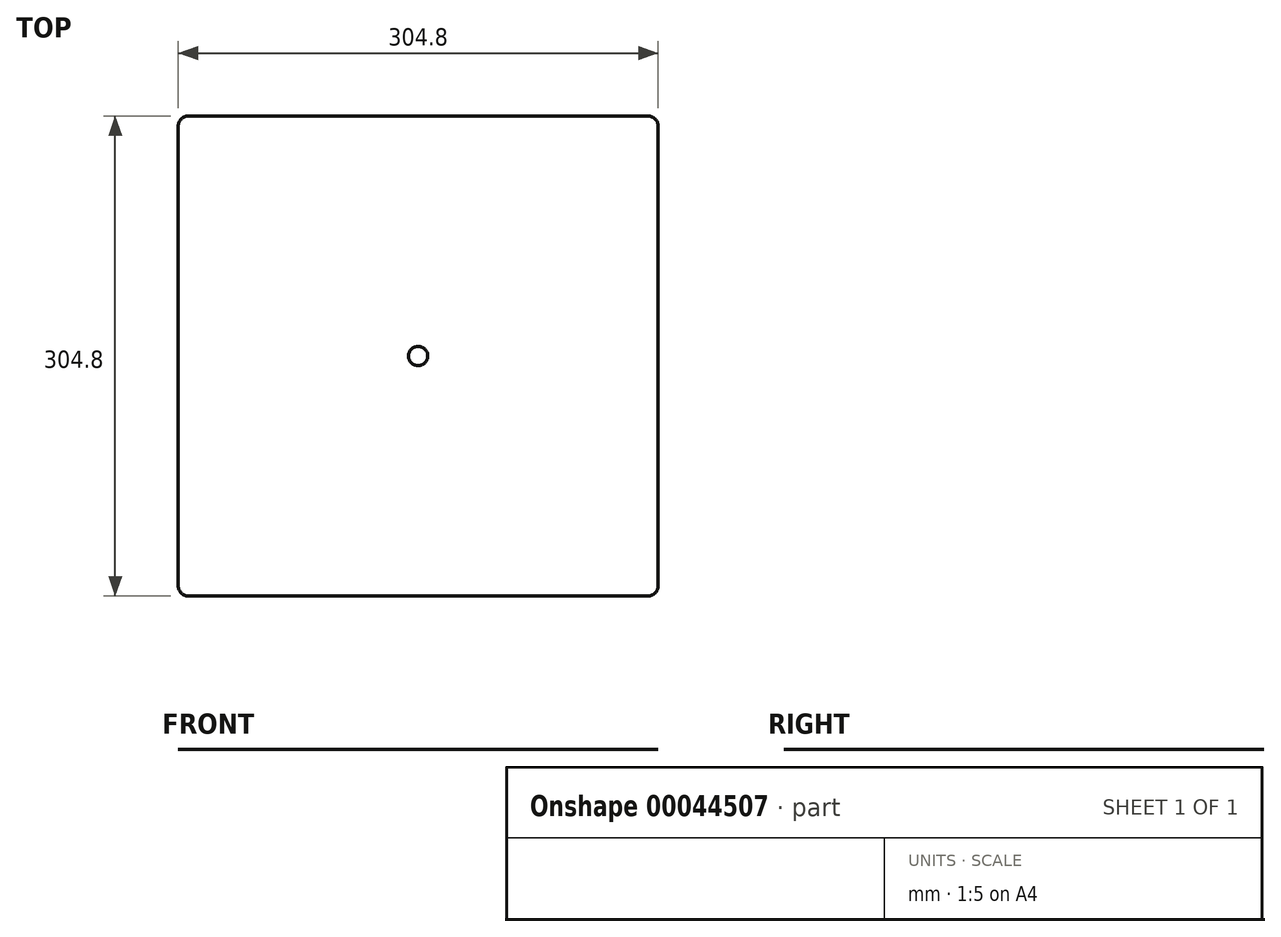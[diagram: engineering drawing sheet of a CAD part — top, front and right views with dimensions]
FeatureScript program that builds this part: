
annotation { "Feature Type Name" : "Feature", "Feature Type Description" : "" }
export const myFeature = defineFeature(function(context is Context, id is Id, definition is map)
    precondition{}
    {
        {
            var Q0;
            Q0=qCreatedBy(makeId("Top.planeOp"),FACE);
            var sketch = newSketch(context, id + "F0", { "sketchPlane" : qUnion([Q0])});
            skLineSegment(sketch, "E0.rect.bottom", {"start": v(-152.4, 152.4) * mm, "end": v(152.4, 152.4) * mm});
            skLineSegment(sketch, "E0.rect.top", {"start": v(-152.4, -152.4) * mm, "end": v(152.4, -152.4) * mm});
            skLineSegment(sketch, "E0.rect.left", {"start": v(-152.4, 152.4) * mm, "end": v(-152.4, -152.4) * mm});
            skLineSegment(sketch, "E0.rect.right", {"start": v(152.4, 152.4) * mm, "end": v(152.4, -152.4) * mm});
            skPoint(sketch, "E0.rect.middle", {"position": v(0, 0) * mm});
            skSolve(sketch);
        }
        {
            var Q0;
            Q0=qSketchRegion(id+"F0",true);
            extrude(context, id + "F1", {"entities" : qUnion([Q0]), "depth" : 1 / 406.4 * mm});
        }
        {
            var Q0;
            Q0=makeQuery(id+"F1.opExtrude","SWEPT_EDGE",EDGE,{"disambiguationData":[OSD([sQuery(id+"F0.wireOp",EDGE,"E0.rect.top"),sQuery(id+"F0.wireOp",EDGE,"E0.rect.left")])]});
            var Q1;
            Q1=makeQuery(id+"F1.opExtrude","SWEPT_EDGE",EDGE,{"disambiguationData":[OSD([sQuery(id+"F0.wireOp",EDGE,"E0.rect.top"),sQuery(id+"F0.wireOp",EDGE,"E0.rect.right")])]});
            var Q2;
            Q2=makeQuery(id+"F1.opExtrude","SWEPT_EDGE",EDGE,{"disambiguationData":[OSD([sQuery(id+"F0.wireOp",EDGE,"E0.rect.bottom"),sQuery(id+"F0.wireOp",EDGE,"E0.rect.right")])]});
            var Q3;
            Q3=makeQuery(id+"F1.opExtrude","SWEPT_EDGE",EDGE,{"disambiguationData":[OSD([sQuery(id+"F0.wireOp",EDGE,"E0.rect.bottom"),sQuery(id+"F0.wireOp",EDGE,"E0.rect.left")])]});
            fillet(context, id + "F2", {"entities" : qUnion([Q0, Q1, Q2, Q3]), "radius" : 6.35 * mm, "allowEdgeOverflow" : false});
        }
        {
            var Q0;
            Q0=makeQuery(id+"F1.opExtrude","CAP_FACE",FACE,{"disambiguationData":[OSD([sQuery(id+"F0.wireOp",EDGE,"E0.rect.bottom"),sQuery(id+"F0.wireOp",EDGE,"E0.rect.top"),sQuery(id+"F0.wireOp",EDGE,"E0.rect.left"),sQuery(id+"F0.wireOp",EDGE,"E0.rect.right")])],"isStart":false});
            var sketch = newSketch(context, id + "F3", { "sketchPlane" : qUnion([Q0])});
            skPoint(sketch, "E1", {"position": v(0, 0) * mm});
            skSolve(sketch);
        }
        {
            var Q0;
            Q0=sQuery(id+"F3.wireOp",VERTEX,"E1");
            var Q1;
            Q1=makeQuery(id+"F1.opExtrude","SWEPT_BODY",BODY,{"disambiguationData":[OSD([sQuery(id+"F0.wireOp",EDGE,"E0.rect.bottom"),sQuery(id+"F0.wireOp",EDGE,"E0.rect.top"),sQuery(id+"F0.wireOp",EDGE,"E0.rect.left"),sQuery(id+"F0.wireOp",EDGE,"E0.rect.right")])]});
            hole(context, id + "F4", {"style" : HoleStyle.C_SINK, "holeDiameter" : 6.2 * mm, "cSinkDiameter" : 12.2 * mm, "endStyle" : HoleEndStyle.THROUGH, "locations" : qUnion([Q0]), "scope" : qUnion([Q1]), "cSinkAngle" : 90 * degree});
        }
    });
